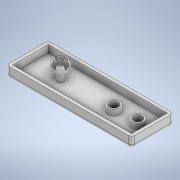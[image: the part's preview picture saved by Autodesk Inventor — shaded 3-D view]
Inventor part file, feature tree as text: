
AUTODESK INVENTOR PART (.ipt)
format: ipt  version: 2021 (Build 250183000, 183)  size: 279,552 bytes
history: native  units: mm
features: sketch x11, extrude x10, fillet x3, revolve x1
ambient origin geometry x8: Origin, YZ Plane, XZ Plane, XY Plane, X Axis, Y Axis, Z Axis, Center Point
bodies: Solid1 (feature_tree)
feature tree (25):
  revolve  "Revolution1"  [1 undecoded]
  extrude  "Extrusion1"  Depth=25.0mm
  fillet  "Fillet1"  [1 undecoded]
  extrude  "Extrusion2"  Depth=3.75mm
  extrude  "Extrusion3"  Depth=50.0mm
  extrude  "Extrusion4"  Depth=50.0mm
  extrude  "Extrusion5"  Depth=50.0mm
  extrude  "Extrusion6"  Depth=5.0mm TaperAngle=0.0deg
  extrude  "Extrusion7"  Depth=17.5mm
  extrude  "Extrusion8"  Depth=5.0mm TaperAngle=0.0deg
  extrude  "Extrusion9"  Depth=5.0mm TaperAngle=0.0deg
  fillet  "Fillet2"  Radius=20.0mm
  fillet  "Fillet3"  Radius=10.0mm
  extrude  "Extrusion10"  Depth=10.0mm TaperAngle=0.0deg
  sketch  "Sketch1"  dims[d0=5.0mm d1=10.0mm]
  sketch  "Sketch2"  dims[d2=25.0mm d3=20.0mm d4=90.0deg]
  sketch  "Sketch3"  dims[d10=7.5mm d11=0.0mm d12=3.75mm]
  sketch  "Sketch4"  dims[d13=50.0mm d14=30.0mm]
  sketch  "Sketch5"  dims[d15=50.0mm d16=30.0mm]
  sketch  "Sketch6"  dims[d17=5.0mm d18=0.0mm d19=50.0mm]
  sketch  "Sketch7"  dims[d20=17.5mm d21=5.0mm d22=0.0mm]
  sketch  "Sketch8"  dims[d23=50.0mm d24=17.5mm]
  sketch  "Sketch9"  dims[d25=5.0mm d26=0.0mm d27=5.0mm d28=0.0mm]
  sketch  "Sketch10"  dims[d29=155.0mm d30=0.0mm d31=5.0mm d32=0.0mm d34=20.0mm d36=10.0mm d37=0.0mm]
  sketch  "Sketch11"  dims[d38=15.0mm d39=10.0mm d40=0.0mm d41=5.0mm d42=5.0mm d47=1.0mm d48=0.0mm d33=5.0mm d35=5.0mm]
note: 2 required parameter values undecoded (feature->parameter linkage not recoverable at this tier; creation-order binding heuristic only, values carry confidence <= 0.55)